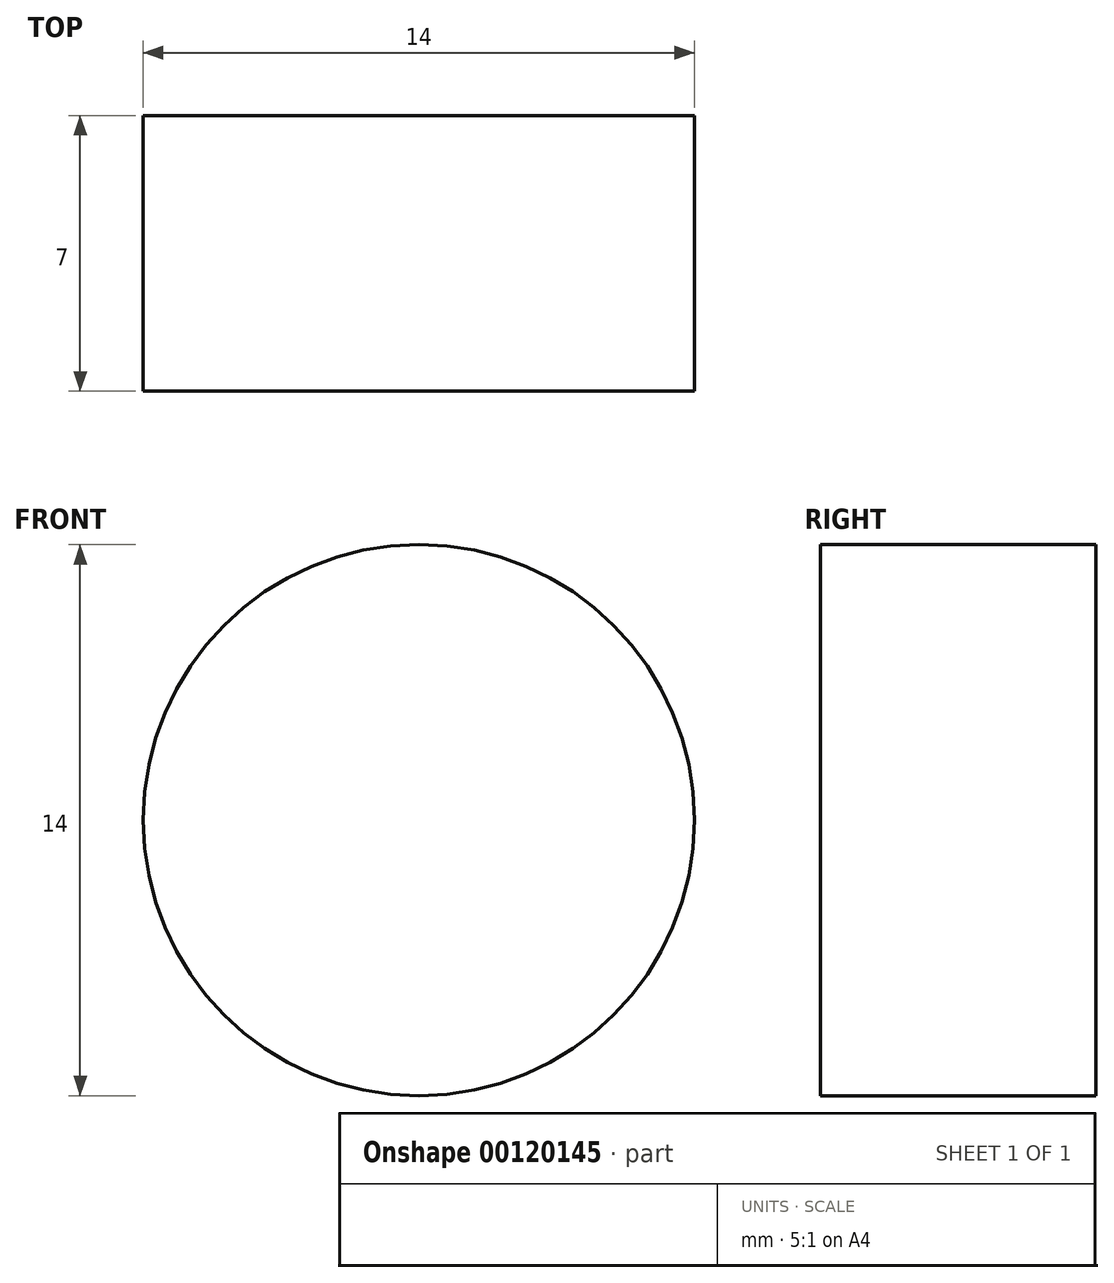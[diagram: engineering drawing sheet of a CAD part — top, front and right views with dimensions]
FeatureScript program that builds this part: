
annotation { "Feature Type Name" : "Feature", "Feature Type Description" : "" }
export const myFeature = defineFeature(function(context is Context, id is Id, definition is map)
    precondition{}
    {
        {
            var Q0;
            Q0=qCreatedBy(makeId("Front.planeOp"),FACE);
            var sketch = newSketch(context, id + "F0", { "sketchPlane" : qUnion([Q0])});
            skCircle(sketch, "E0", {"center": v(0, 0) * mm, "radius": 7 * mm});
            skSolve(sketch);
        }
        {
            var Q0;
            Q0 = qSketchRegion(id + "F0", true);
            extrude(context, id + "F1", {"entities" : qUnion([Q0]), "depth" : 7 * mm});
        }
    });
